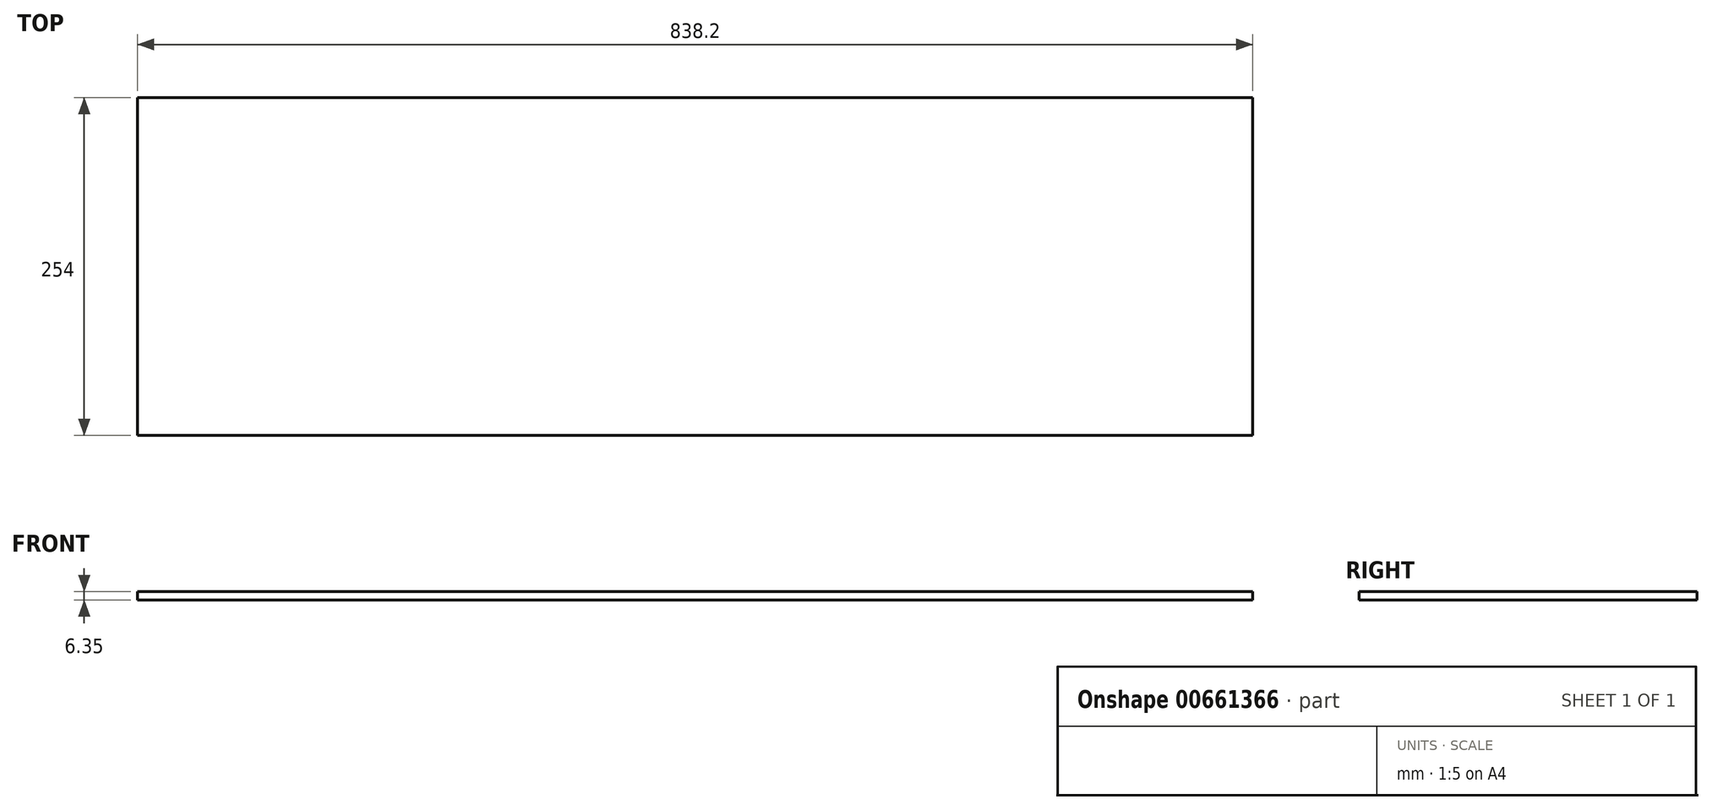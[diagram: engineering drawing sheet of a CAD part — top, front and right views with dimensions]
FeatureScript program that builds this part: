
annotation { "Feature Type Name" : "Feature", "Feature Type Description" : "" }
export const myFeature = defineFeature(function(context is Context, id is Id, definition is map)
    precondition{}
    {
        {
            var Q0;
            Q0=qCreatedBy(makeId("Top.planeOp"),FACE);
            var sketch = newSketch(context, id + "F0", { "sketchPlane" : qUnion([Q0])});
            skLineSegment(sketch, "E0.bottom", {"start": v(-754.7, 206.32) * mm, "end": v(83.5, 206.32) * mm});
            skLineSegment(sketch, "E0.top", {"start": v(-754.7, -47.68) * mm, "end": v(83.5, -47.68) * mm});
            skLineSegment(sketch, "E0.left", {"start": v(-754.7, 206.32) * mm, "end": v(-754.7, -47.68) * mm});
            skLineSegment(sketch, "E0.right", {"start": v(83.5, 206.32) * mm, "end": v(83.5, -47.68) * mm});
            skSolve(sketch);
        }
        {
            var Q0;
            Q0=makeQuery(id+"F0.imprint","IMPRINT",FACE,{"disambiguationData":[TD([[makeQuery(id+"F0.imprint","IMPRINT",EDGE,{"derivedFrom":sQuery(id+"F0.wireOp",EDGE,"E0.bottom")}),-1.0]])]});
            extrude(context, id + "F1", {"entities" : qUnion([Q0]), "depth" : 6.35 * mm, "offsetDistance" : 25.4 * mm});
        }
    });
